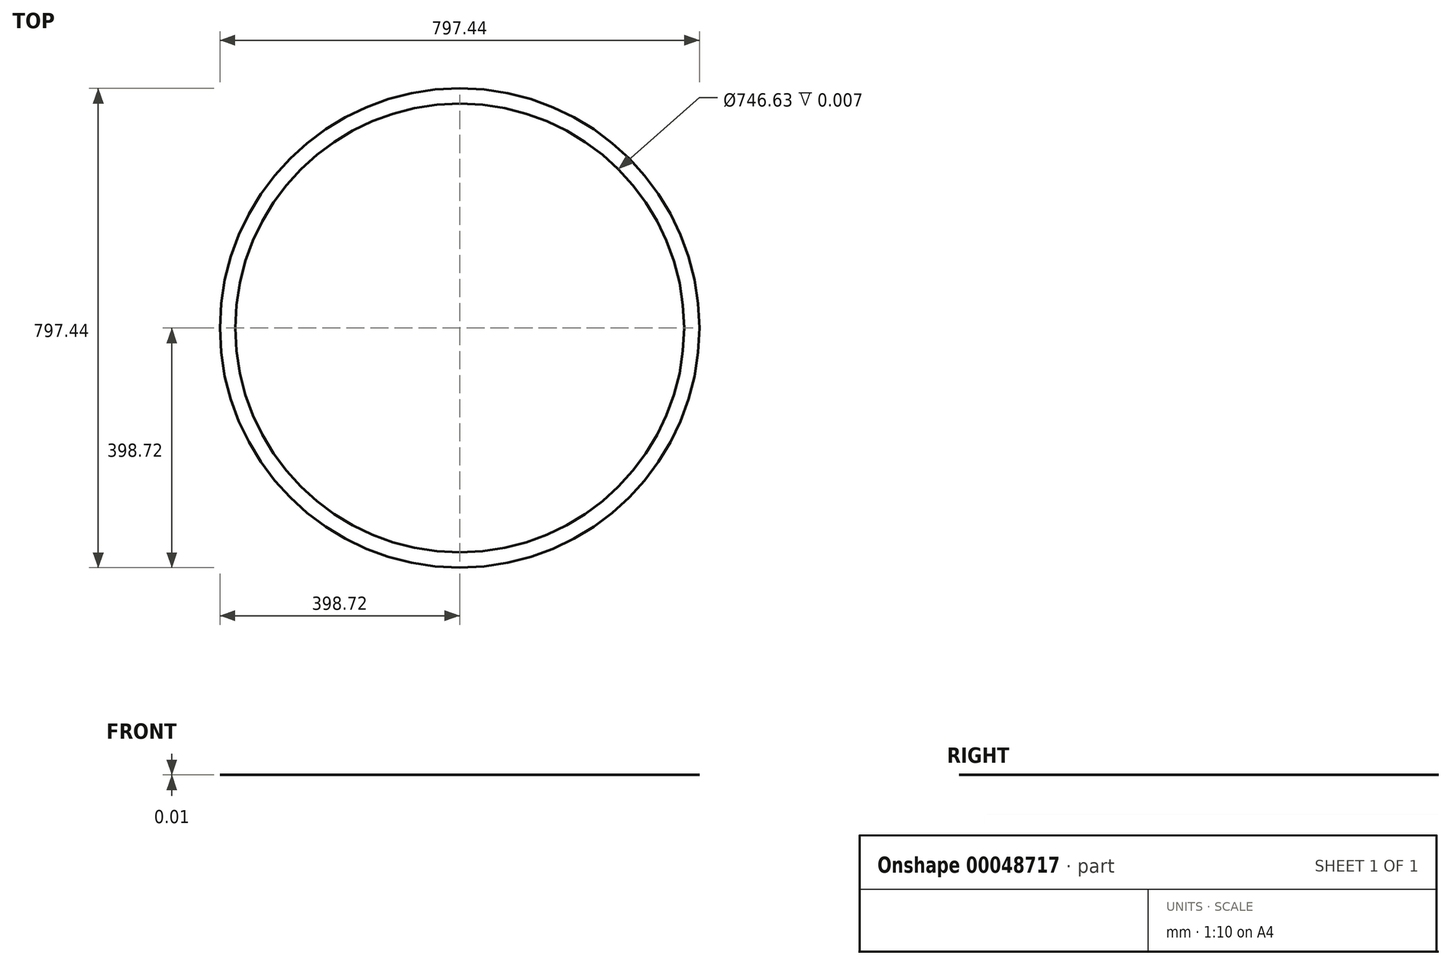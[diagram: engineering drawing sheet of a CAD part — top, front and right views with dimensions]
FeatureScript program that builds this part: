
annotation { "Feature Type Name" : "Feature", "Feature Type Description" : "" }
export const myFeature = defineFeature(function(context is Context, id is Id, definition is map)
    precondition{}
    {
        {
            var Q0;
            Q0=qCreatedBy(makeId("Top.planeOp"),FACE);
            var sketch = newSketch(context, id + "F0", { "sketchPlane" : qUnion([Q0])});
            skCircle(sketch, "E0", {"center": v(0, 0) * mm, "radius": 398.72 * mm});
            skCircle(sketch, "E1", {"center": v(0, 0) * mm, "radius": 373.32 * mm});
            skSolve(sketch);
        }
        {
            var Q0;
            Q0=makeQuery(id+"F0.imprint","IMPRINT",FACE,{"disambiguationData":[TD([[makeQuery(id+"F0.imprint","IMPRINT",EDGE,{"derivedFrom":sQuery(id+"F0.wireOp",EDGE,"E0")}),1.0]])]});
            extrude(context, id + "F1", {"entities" : qUnion([Q0]), "depth" : 3 / 406.4 * mm});
        }
    });
